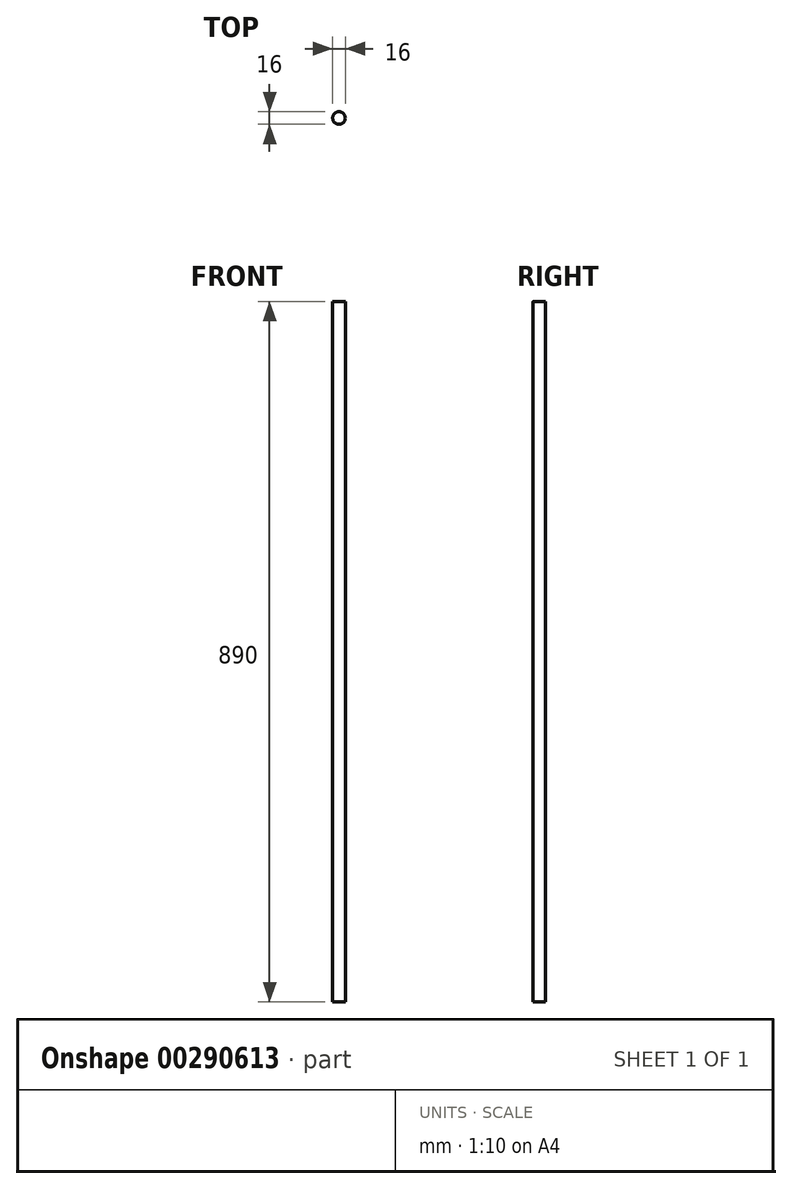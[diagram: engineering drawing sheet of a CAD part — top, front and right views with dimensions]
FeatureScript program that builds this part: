
annotation { "Feature Type Name" : "Feature", "Feature Type Description" : "" }
export const myFeature = defineFeature(function(context is Context, id is Id, definition is map)
    precondition{}
    {
        {
            var Q0;
            Q0=qCreatedBy(makeId("Top.planeOp"),FACE);
            var sketch = newSketch(context, id + "F0", { "sketchPlane" : qUnion([Q0])});
            skCircle(sketch, "E0", {"center": v(0, 0) * mm, "radius": 8 * mm});
            skSolve(sketch);
        }
        {
            var Q0;
            Q0 = qSketchRegion(id + "F0", true);
            extrude(context, id + "F1", {"entities" : qUnion([Q0]), "depth" : 890 * mm});
        }
    });
